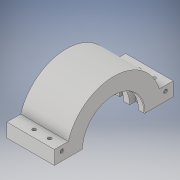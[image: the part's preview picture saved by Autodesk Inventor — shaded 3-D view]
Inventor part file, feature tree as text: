
AUTODESK INVENTOR PART (.ipt)
format: ipt  version: 2019 (Build 230136000, 136)  size: 538,112 bytes
history: native  units: mm
features: sketch x26, extrude x21, mirror x13, plane x12, projected_geometry x11, other x4, fillet x4, hole x3
ambient origin geometry x8: Origin, YZ Plane, XZ Plane, XY Plane, X Axis, Y Axis, Z Axis, Center Point
bodies: Body1 (feature_tree)
feature tree (94):
  other  "實體1"
  extrude  "擠出1"  Depth=123.43mm
  plane  "工作平面2"
  extrude  "擠出3"  Depth=160.0mm
  plane  "工作平面3"
  extrude  "擠出4"  Depth=120.0mm TaperAngle=0.0deg
  extrude  "擠出5"  [1 undecoded]
  plane  "工作平面4"
  extrude  "擠出7"  Depth=130.0mm
  plane  "工作平面5"
  extrude  "擠出9"  Depth=15.0mm TaperAngle=0.0deg
  extrude  "擠出10"  [1 undecoded]
  extrude  "擠出11"  Depth=140.0mm
  extrude  "擠出12"  Depth=10.0mm TaperAngle=0.0deg
  mirror  "鏡射1"
  fillet  "圓角2"  Radius=10.0mm
  fillet  "圓角3"  Radius=10.0mm
  sketch  "草圖16"
  plane  "工作平面7"
  mirror  "鏡射2"
  fillet  "圓角5"  [1 undecoded]
  fillet  "圓角6"  Radius=10.0mm
  plane  "工作平面8"
  plane  "工作平面9"
  sketch  "草圖20"
  extrude  "擠出15"  [1 undecoded]
  plane  "工作平面10"
  extrude  "擠出16"  Depth=10.0mm
  extrude  "擠出17"  Depth=10.0mm TaperAngle=0.0deg
  plane  "工作平面11"
  extrude  "擠出19"  Depth=10.0mm TaperAngle=0.0deg
  extrude  "擠出20"  Depth=160.0mm
  mirror  "鏡射3"
  mirror  "鏡射4"
  extrude  "擠出21"  Depth=80.0mm
  mirror  "鏡射7"
  plane  "工作平面15"
  mirror  "鏡射9"
  hole  "孔2"  [1 undecoded]
  mirror  "鏡射10"
  mirror  "鏡射11"
  hole  "孔3"  [1 undecoded]
  mirror  "鏡射12"
  mirror  "鏡射13"
  extrude  "擠出22"  Depth=160.0mm
  extrude  "擠出23"  Depth=120.0mm TaperAngle=0.0deg
  extrude  "擠出24"  Depth=120.0mm TaperAngle=0.0deg
  extrude  "擠出25"  Depth=25.0mm
  extrude  "擠出27"  Depth=20.0mm
  extrude  "擠出28"  Depth=2.0mm
  mirror  "鏡射14"
  plane  "工作平面17"
  hole  "孔4"  [1 undecoded]
  mirror  "鏡射15"
  mirror  "鏡射16"
  other  "分割2"
  other  "分割3"
  other  "分割4"
  sketch  "草圖1"
  sketch  "草圖4"
  sketch  "草圖6"
  sketch  "草圖7"
  projected_geometry  "投影迴路1"
  sketch  "草圖9"
  projected_geometry  "投影迴路4"
  sketch  "草圖11"
  sketch  "草圖12"
  projected_geometry  "投影迴路6"
  sketch  "草圖13"
  projected_geometry  "投影迴路7"
  sketch  "草圖14"
  plane  "工作平面6"
  sketch  "草圖17"
  projected_geometry  "投影迴路8"
  sketch  "草圖24"
  projected_geometry  "投影迴路11"
  sketch  "草圖25"
  sketch  "草圖26"
  sketch  "草圖27"
  sketch  "草圖28"
  sketch  "草圖29"
  projected_geometry  "投影迴路12"
  sketch  "草圖30"
  sketch  "草圖31"
  sketch  "草圖32"
  projected_geometry  "投影迴路13"
  projected_geometry  "投影迴路14"
  projected_geometry  "投影迴路15"
  sketch  "草圖33"
  sketch  "草圖34"
  sketch  "草圖35"
  projected_geometry  "投影迴路16"
  sketch  "草圖36"
  sketch  "草圖37"
note: 7 required parameter values undecoded (feature->parameter linkage not recoverable at this tier; creation-order binding heuristic only, values carry confidence <= 0.55)
